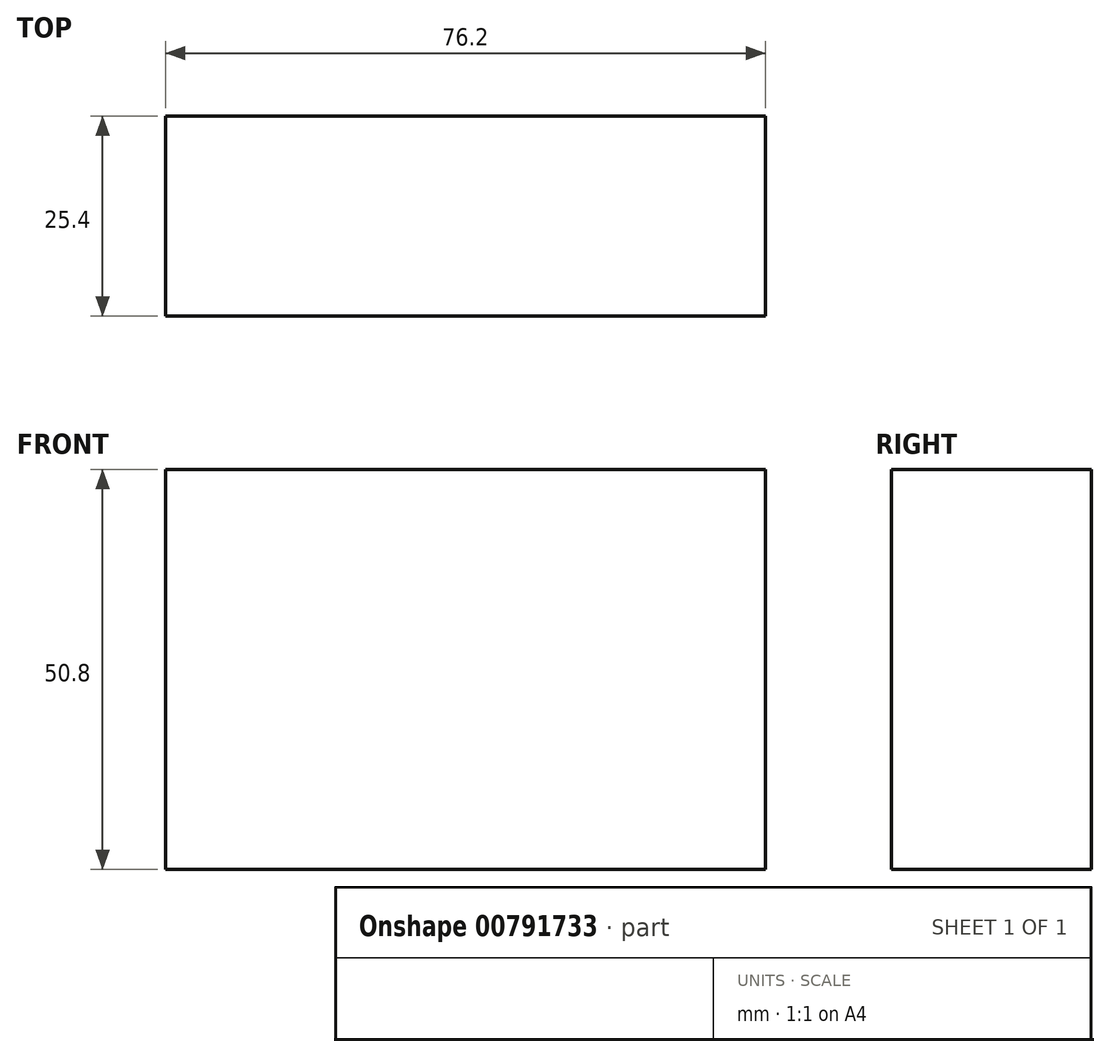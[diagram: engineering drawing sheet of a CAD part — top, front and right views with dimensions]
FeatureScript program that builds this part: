
annotation { "Feature Type Name" : "Feature", "Feature Type Description" : "" }
export const myFeature = defineFeature(function(context is Context, id is Id, definition is map)
    precondition{}
    {
        {
            var Q0;
            Q0=qCreatedBy(makeId("Front.planeOp"),FACE);
            var sketch = newSketch(context, id + "F0", { "sketchPlane" : qUnion([Q0])});
            skLineSegment(sketch, "E0.bottom", {"start": v(0, 0) * mm, "end": v(-76.2, 0) * mm});
            skLineSegment(sketch, "E0.top", {"start": v(0, 50.8) * mm, "end": v(-76.2, 50.8) * mm});
            skLineSegment(sketch, "E0.left", {"start": v(0, 0) * mm, "end": v(0, 50.8) * mm});
            skLineSegment(sketch, "E0.right", {"start": v(-76.2, 0) * mm, "end": v(-76.2, 50.8) * mm});
            skSolve(sketch);
        }
        {
            var Q0;
            Q0=makeQuery(id+"F0.imprint","IMPRINT",FACE,{"disambiguationData":[TD([[makeQuery(id+"F0.imprint","IMPRINT",EDGE,{"derivedFrom":sQuery(id+"F0.wireOp",EDGE,"E0.bottom")}),-1.0]])]});
            extrude(context, id + "F1", {"entities" : qUnion([Q0]), "depth" : 25.4 * mm, "offsetDistance" : 25.4 * mm});
        }
    });
